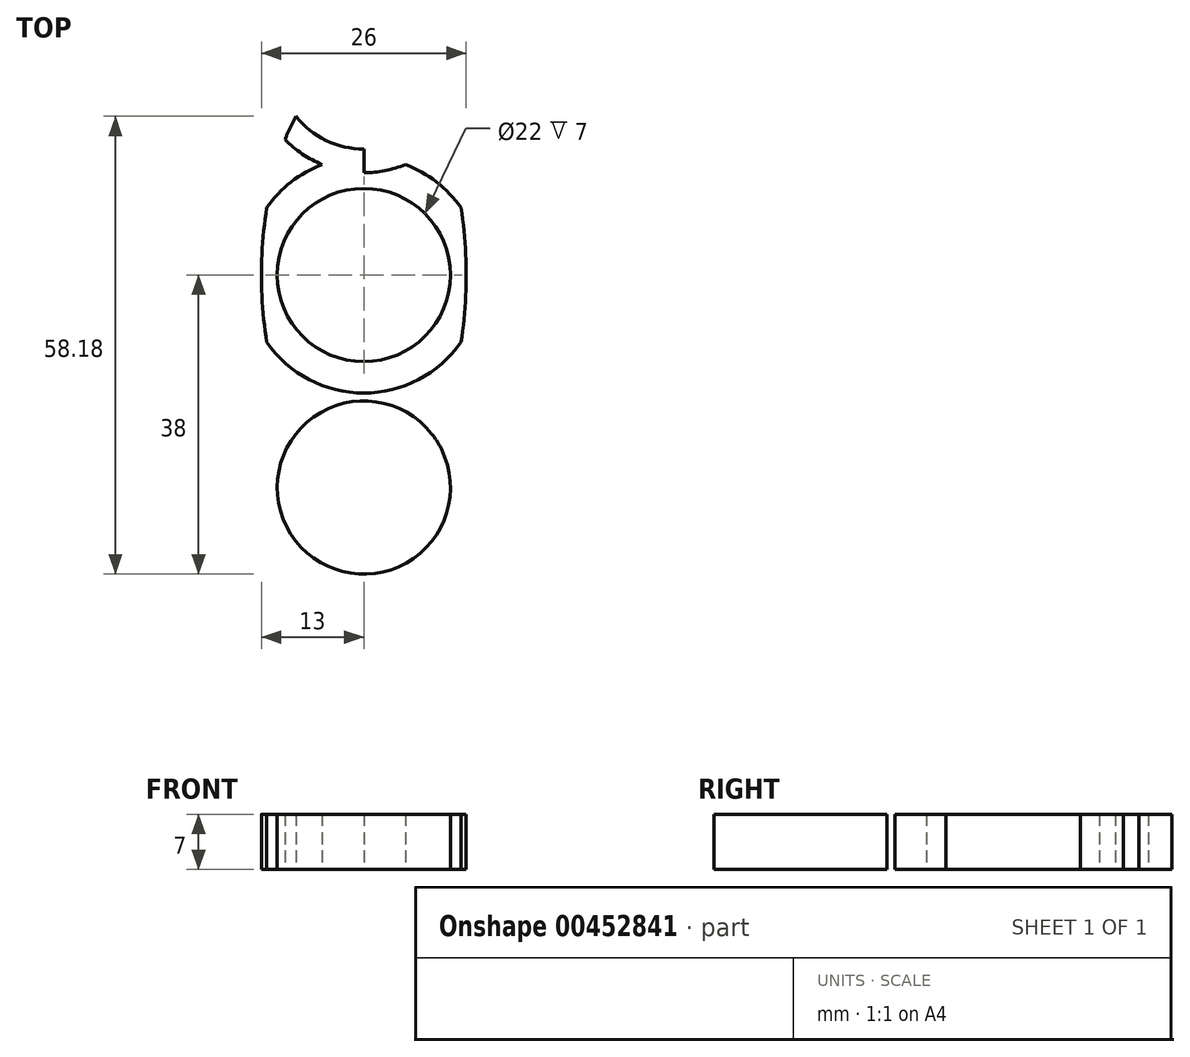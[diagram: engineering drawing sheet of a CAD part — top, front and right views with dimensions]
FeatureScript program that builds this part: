
annotation { "Feature Type Name" : "Feature", "Feature Type Description" : "" }
export const myFeature = defineFeature(function(context is Context, id is Id, definition is map)
    precondition{}
    {
        {
            var Q0;
            Q0=qCreatedBy(makeId("Top.planeOp"),FACE);
            var sketch = newSketch(context, id + "F0", { "sketchPlane" : qUnion([Q0])});
            skCircle(sketch, "E0", {"center": v(0, 0) * mm, "radius": 11 * mm});
            skArc(sketch, "E1.0", {"start": v(-12.33, -8.54) * mm, "mid": v(0, -15) * mm, "end": v(12.33, -8.54) * mm});
            skCircle(sketch, "E2.0", {"center": v(0, 0) * mm, "radius": 13 * mm});
            skPoint(sketch, "E3", {"position": v(13, 0) * mm});
            skPoint(sketch, "E4", {"position": v(-13, 0) * mm});
            skLineSegment(sketch, "E5", {"start": v(0, 0) * mm, "end": v(0, 27) * mm});
            skPoint(sketch, "E6", {"position": v(15, 0) * mm});
            skEllipticalArc(sketch, "E7", {});
            skFitSpline(sketch, "E8.0", {"points": [v(1.7, 28.88) * mm, v(0, 29.06) * mm, v(-1.7, 28.88) * mm, v(-3.33, 28.37) * mm, v(-4.87, 27.57) * mm, v(-6.3, 26.5) * mm, v(-7.62, 25.2) * mm, v(-8.85, 23.67) * mm, v(-9.8, 22.22) * mm, v(-10.5, 20.96) * mm, v(-11, 19.97) * mm, v(-11.48, 18.93) * mm, v(-12.07, 17.5) * mm, v(-12.74, 15.61) * mm, v(-13.43, 13.23) * mm, v(-14, 10.74) * mm, v(-14.44, 8.16) * mm, v(-14.76, 5.5) * mm, v(-14.92, 3.23) * mm, v(-14.99, 1.39) * mm, v(-15, 0) * mm, v(-14.99, -1.39) * mm, v(-14.92, -3.23) * mm, v(-14.76, -5.5) * mm, v(-14.44, -8.16) * mm, v(-14, -10.74) * mm, v(-13.43, -13.23) * mm, v(-12.74, -15.61) * mm, v(-12.07, -17.5) * mm, v(-11.48, -18.93) * mm, v(-11, -19.97) * mm, v(-10.5, -20.96) * mm, v(-9.8, -22.22) * mm, v(-8.85, -23.67) * mm, v(-7.62, -25.2) * mm, v(-6.3, -26.5) * mm, v(-4.87, -27.57) * mm, v(-3.33, -28.37) * mm, v(-1.7, -28.88) * mm, v(0, -29.06) * mm, v(1.7, -28.88) * mm, v(3.33, -28.37) * mm, v(4.87, -27.57) * mm, v(6.3, -26.5) * mm, v(7.62, -25.2) * mm, v(8.85, -23.67) * mm, v(9.8, -22.22) * mm, v(10.5, -20.96) * mm, v(11, -19.97) * mm, v(11.48, -18.93) * mm, v(12.07, -17.5) * mm, v(12.74, -15.61) * mm, v(13.43, -13.23) * mm, v(14, -10.74) * mm, v(14.44, -8.16) * mm, v(14.76, -5.5) * mm, v(14.92, -3.23) * mm, v(14.99, -1.39) * mm, v(15, 0) * mm, v(14.99, 1.39) * mm, v(14.92, 3.23) * mm, v(14.76, 5.5) * mm, v(14.44, 8.16) * mm, v(14, 10.74) * mm, v(13.43, 13.23) * mm, v(12.74, 15.61) * mm, v(12.07, 17.5) * mm, v(11.48, 18.93) * mm, v(11, 19.97) * mm, v(10.5, 20.96) * mm, v(9.8, 22.22) * mm, v(8.85, 23.67) * mm, v(7.62, 25.2) * mm, v(6.3, 26.5) * mm, v(4.87, 27.57) * mm, v(3.33, 28.37) * mm, v(1.7, 28.88) * mm, v(0, 29.06) * mm, v(-1.7, 28.88) * mm]});
            skArc(sketch, "E9", {"start": v(9.85, 22.1) * mm, "mid": v(0, 38) * mm, "end": v(-9.85, 22.1) * mm});
            skArc(sketch, "E10.0", {"start": v(11.46, 18.95) * mm, "mid": v(0, 41) * mm, "end": v(-11.46, 18.95) * mm});
            skArc(sketch, "E11.trimOffspring", {"start": v(-8.63, 20.18) * mm, "mid": v(0, 16) * mm, "end": v(8.63, 20.18) * mm});
            skArc(sketch, "E12.trimOffspring", {"start": v(-10.01, 17.22) * mm, "mid": v(0, 13) * mm, "end": v(10.01, 17.22) * mm});
            skArc(sketch, "E13.trimOffspring", {"start": v(12.33, 8.54) * mm, "mid": v(9.23, 11.82) * mm, "end": v(5.29, 14.04) * mm});
            skArc(sketch, "E14.trimOffspring", {"start": v(-5.29, 14.04) * mm, "mid": v(-9.23, 11.82) * mm, "end": v(-12.33, 8.54) * mm});
            skArc(sketch, "E15.MirrorCS", {"start": v(-10.01, -17.22) * mm, "mid": v(0, -13) * mm, "end": v(10.01, -17.22) * mm});
            skArc(sketch, "E16.MirrorCS", {"start": v(-8.63, -20.18) * mm, "mid": v(0, -16) * mm, "end": v(8.63, -20.18) * mm});
            skArc(sketch, "E17.MirrorCS", {"start": v(9.85, -22.1) * mm, "mid": v(0, -38) * mm, "end": v(-9.85, -22.1) * mm});
            skArc(sketch, "E18.MirrorCS", {"start": v(11.46, -18.95) * mm, "mid": v(0, -41) * mm, "end": v(-11.46, -18.95) * mm});
            skArc(sketch, "E19", {"start": v(-9.85, 22.1) * mm, "mid": v(-9.29, 21.1) * mm, "end": v(-8.63, 20.18) * mm});
            skEllipticalArc(sketch, "E20.trimOffspring", {});
            skArc(sketch, "E21", {"start": v(8.63, 20.18) * mm, "mid": v(9.29, 21.1) * mm, "end": v(9.85, 22.1) * mm});
            skFitSpline(sketch, "E22.trimOffspring", {"points": [v(1.7, 28.88) * mm, v(0, 29.06) * mm, v(-1.7, 28.88) * mm, v(-3.33, 28.37) * mm, v(-4.87, 27.57) * mm, v(-6.3, 26.5) * mm, v(-7.62, 25.2) * mm, v(-8.85, 23.67) * mm, v(-9.8, 22.22) * mm, v(-10.5, 20.96) * mm, v(-11, 19.97) * mm, v(-11.48, 18.93) * mm, v(-12.07, 17.5) * mm, v(-12.74, 15.61) * mm, v(-13.43, 13.23) * mm, v(-14, 10.74) * mm, v(-14.44, 8.16) * mm, v(-14.76, 5.5) * mm, v(-14.92, 3.23) * mm, v(-14.99, 1.39) * mm, v(-15, 0) * mm, v(-14.99, -1.39) * mm, v(-14.92, -3.23) * mm, v(-14.76, -5.5) * mm, v(-14.44, -8.16) * mm, v(-14, -10.74) * mm, v(-13.43, -13.23) * mm, v(-12.74, -15.61) * mm, v(-12.07, -17.5) * mm, v(-11.48, -18.93) * mm, v(-11, -19.97) * mm, v(-10.5, -20.96) * mm, v(-9.8, -22.22) * mm, v(-8.85, -23.67) * mm, v(-7.62, -25.2) * mm, v(-6.3, -26.5) * mm, v(-4.87, -27.57) * mm, v(-3.33, -28.37) * mm, v(-1.7, -28.88) * mm, v(0, -29.06) * mm, v(1.7, -28.88) * mm, v(3.33, -28.37) * mm, v(4.87, -27.57) * mm, v(6.3, -26.5) * mm, v(7.62, -25.2) * mm, v(8.85, -23.67) * mm, v(9.8, -22.22) * mm, v(10.5, -20.96) * mm, v(11, -19.97) * mm, v(11.48, -18.93) * mm, v(12.07, -17.5) * mm, v(12.74, -15.61) * mm, v(13.43, -13.23) * mm, v(14, -10.74) * mm, v(14.44, -8.16) * mm, v(14.76, -5.5) * mm, v(14.92, -3.23) * mm, v(14.99, -1.39) * mm, v(15, 0) * mm, v(14.99, 1.39) * mm, v(14.92, 3.23) * mm, v(14.76, 5.5) * mm, v(14.44, 8.16) * mm, v(14, 10.74) * mm, v(13.43, 13.23) * mm, v(12.74, 15.61) * mm, v(12.07, 17.5) * mm, v(11.48, 18.93) * mm, v(11, 19.97) * mm, v(10.5, 20.96) * mm, v(9.8, 22.22) * mm, v(8.85, 23.67) * mm, v(7.62, 25.2) * mm, v(6.3, 26.5) * mm, v(4.87, 27.57) * mm, v(3.33, 28.37) * mm, v(1.7, 28.88) * mm, v(0, 29.06) * mm, v(-1.7, 28.88) * mm]});
            skArc(sketch, "E23", {"start": v(-9.85, -22.1) * mm, "mid": v(-9.29, -21.1) * mm, "end": v(-8.63, -20.18) * mm});
            skArc(sketch, "E24", {"start": v(8.63, -20.18) * mm, "mid": v(9.29, -21.1) * mm, "end": v(9.85, -22.1) * mm});
            const initialGuessF0  = {"E7": [0, 0, 1, 0, 0.013, 0.027, 2.2971845357045924, 3.833037989963207], "E20.trimOffspring": [0, 0, 1, 0, 0.013, 0.027, 5.591739970806172, 0.6914453363734143]};
            skSetInitialGuess(sketch, initialGuessF0);
            skSolve(sketch);
        }
        {
            var Q0;
            {var subQ0=sQuery(id+"F0.wireOp",EDGE,"E12.trimOffspring");var subQ1=sQuery(id+"F0.wireOp",EDGE,"E7");var subQ2=makeQuery(id+"F0.imprint","INTERSECT",VERTEX,{"derivedFrom":[subQ1,subQ0]});Q0=makeQuery(id+"F0.imprint","IMPRINT",FACE,{"disambiguationData":[TD([[makeQuery(id+"F0.imprint","IMPRINT",EDGE,{"disambiguationData":[TD([[subQ2,-1.0]])],"derivedFrom":subQ0}),1.0]])]});}
            var Q1;
            Q1=makeQuery(id+"F0.imprint","IMPRINT",FACE,{"disambiguationData":[TD([[makeQuery(id+"F0.imprint","IMPRINT",EDGE,{"derivedFrom":sQuery(id+"F0.wireOp",EDGE,"E16.MirrorCS")}),1.0]])]});
            var Q2;
            {var subQ0=sQuery(id+"F0.wireOp",EDGE,"E9");Q2=makeQuery(id+"F0.imprint","IMPRINT",FACE,{"disambiguationData":[TD([[makeQuery(id+"F0.imprint","IMPRINT",EDGE,{"derivedFrom":subQ0}),-1.0]])]});}
            var Q3;
            Q3=makeQuery(id+"F0.imprint","IMPRINT",FACE,{"disambiguationData":[TD([[makeQuery(id+"F0.imprint","IMPRINT",EDGE,{"derivedFrom":sQuery(id+"F0.wireOp",EDGE,"E0")}),-1.0]])]});
            var Q4;
            {var subQ5=sQuery(id+"F0.wireOp",EDGE,"E14.trimOffspring");Q4=makeQuery(id+"F0.imprint","IMPRINT",FACE,{"disambiguationData":[TD([[makeQuery(id+"F0.imprint","IMPRINT",EDGE,{"derivedFrom":subQ5}),1.0]])]});}
            var Q5;
            {var subQ5=sQuery(id+"F0.wireOp",EDGE,"E13.trimOffspring");Q5=makeQuery(id+"F0.imprint","IMPRINT",FACE,{"disambiguationData":[TD([[makeQuery(id+"F0.imprint","IMPRINT",EDGE,{"derivedFrom":subQ5}),1.0]])]});}
            var Q6;
            {var subQ0=sQuery(id+"F0.wireOp",EDGE,"E20.trimOffspring");var subQ1=sQuery(id+"F0.wireOp",EDGE,"E1.0");var subQ2=makeQuery(id+"F0.imprint","INTERSECT",VERTEX,{"derivedFrom":[subQ1,subQ0]});Q6=makeQuery(id+"F0.imprint","IMPRINT",FACE,{"disambiguationData":[TD([[makeQuery(id+"F0.imprint","IMPRINT",EDGE,{"disambiguationData":[TD([[subQ2,1.0]])],"derivedFrom":subQ1}),1.0]])]});}
            var Q7;
            {var subQ0=sQuery(id+"F0.wireOp",EDGE,"E15.MirrorCS");var subQ1=sQuery(id+"F0.wireOp",EDGE,"E1.0");var subQ2=makeQuery(id+"F0.imprint","INTERSECT",VERTEX,{"disambiguationData":[OD(0.0)],"derivedFrom":[subQ1,subQ0]});Q7=makeQuery(id+"F0.imprint","IMPRINT",FACE,{"disambiguationData":[TD([[makeQuery(id+"F0.imprint","IMPRINT",EDGE,{"disambiguationData":[TD([[subQ2,-1.0]])],"derivedFrom":subQ1}),1.0]])]});}
            var Q8;
            {var subQ0=sQuery(id+"F0.wireOp",EDGE,"E7");var subQ1=sQuery(id+"F0.wireOp",EDGE,"E1.0");var subQ2=makeQuery(id+"F0.imprint","INTERSECT",VERTEX,{"derivedFrom":[subQ1,subQ0]});Q8=makeQuery(id+"F0.imprint","IMPRINT",FACE,{"disambiguationData":[TD([[makeQuery(id+"F0.imprint","IMPRINT",EDGE,{"disambiguationData":[TD([[subQ2,-1.0]])],"derivedFrom":subQ1}),1.0]])]});}
            var Q9;
            {var subQ0=sQuery(id+"F0.wireOp",EDGE,"E17.MirrorCS");Q9=makeQuery(id+"F0.imprint","IMPRINT",FACE,{"disambiguationData":[TD([[makeQuery(id+"F0.imprint","IMPRINT",EDGE,{"derivedFrom":subQ0}),1.0]])]});}
            extrude(context, id + "F1", {"entities" : qUnion([Q0, Q1, Q2, Q3, Q4, Q5, Q6, Q7, Q8, Q9]), "endBound" : BoundingType.SYMMETRIC, "depth" : 7 * mm});
        }
    });
